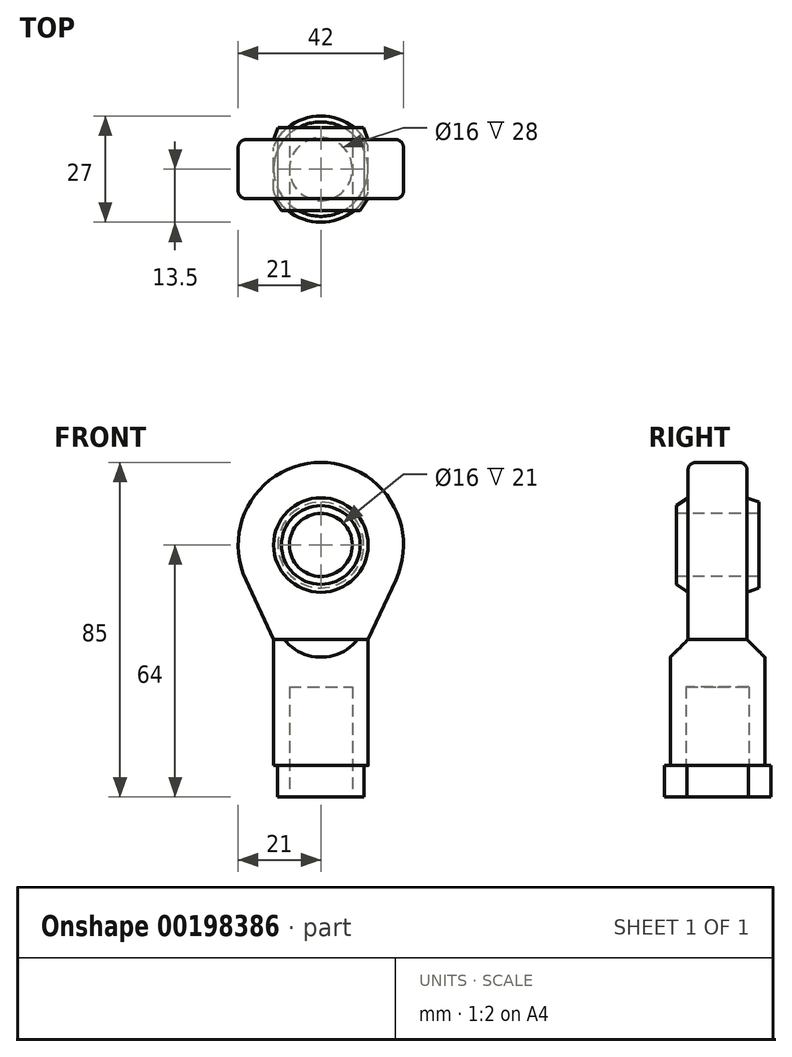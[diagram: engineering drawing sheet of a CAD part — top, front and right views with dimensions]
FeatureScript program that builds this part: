
annotation { "Feature Type Name" : "Feature", "Feature Type Description" : "" }
export const myFeature = defineFeature(function(context is Context, id is Id, definition is map)
    precondition{}
    {
        {
            var Q0;
            Q0=qCreatedBy(makeId("Top.planeOp"),FACE);
            var sketch = newSketch(context, id + "F0", { "sketchPlane" : qUnion([Q0])});
            skCircle(sketch, "E0", {"center": v(0, 0) * mm, "radius": 12 * mm});
            skSolve(sketch);
        }
        {
            var Q0;
            Q0 = qSketchRegion(id + "F0", true);
            extrude(context, id + "F1", {"entities" : qUnion([Q0]), "depth" : 64 * mm});
        }
        {
            var Q0;
            Q0=qCreatedBy(makeId("Top.planeOp"),FACE);
            var sketch = newSketch(context, id + "F2", { "sketchPlane" : qUnion([Q0])});
            skCircle(sketch, "E1", {"center": v(0, 0) * mm, "radius": 13.5 * mm});
            skSolve(sketch);
        }
        {
            var Q0;
            Q0 = qSketchRegion(id + "F2", true);
            extrude(context, id + "F3", {"entities" : qUnion([Q0]), "operationType" : NewBodyOperationType.ADD, "depth" : 8 * mm});
        }
        {
            var Q0;
            Q0=qCreatedBy(makeId("Front.planeOp"),FACE);
            var sketch = newSketch(context, id + "F4", { "sketchPlane" : qUnion([Q0])});
            skArc(sketch, "E2", {"start": v(19.04, 55.15) * mm, "mid": v(0, 85) * mm, "end": v(-19.04, 55.15) * mm});
            skLineSegment(sketch, "E3", {"start": v(12, 40) * mm, "end": v(12, 8) * mm});
            skLineSegment(sketch, "E4", {"start": v(-12, 8) * mm, "end": v(-12, 40) * mm});
            skLineSegment(sketch, "E5", {"start": v(-12, 40) * mm, "end": v(-19.04, 55.15) * mm});
            skLineSegment(sketch, "E6", {"start": v(12, 40) * mm, "end": v(19.04, 55.15) * mm});
            skLineSegment(sketch, "E7", {"start": v(-12, 40) * mm, "end": v(12, 40) * mm});
            skPoint(sketch, "E8.orphan", {"position": v(12, 64) * mm});
            skPoint(sketch, "E9.orphan", {"position": v(-12, 64) * mm});
            skSolve(sketch);
        }
        {
            var Q0;
            Q0 = qSketchRegion(id + "F4", true);
            extrude(context, id + "F5", {"entities" : qUnion([Q0]), "operationType" : NewBodyOperationType.ADD, "endBound" : BoundingType.SYMMETRIC, "depth" : 15 * mm});
        }
        {
            var Q0;
            Q0=qCreatedBy(makeId("Right.planeOp"),FACE);
            var sketch = newSketch(context, id + "F6", { "sketchPlane" : qUnion([Q0])});
            skLineSegment(sketch, "E10", {"start": v(-7.5, 64) * mm, "end": v(-7.5, 40) * mm});
            skLineSegment(sketch, "E11", {"start": v(-7.5, 40) * mm, "end": v(-12, 35.5) * mm});
            skLineSegment(sketch, "E12", {"start": v(-12, 35.5) * mm, "end": v(-12, 64) * mm});
            skLineSegment(sketch, "E13", {"start": v(-12, 64) * mm, "end": v(-7.5, 64) * mm});
            skLineSegment(sketch, "E14", {"start": v(7.5, 64) * mm, "end": v(7.5, 40) * mm});
            skLineSegment(sketch, "E15", {"start": v(7.5, 40) * mm, "end": v(12, 35.5) * mm});
            skLineSegment(sketch, "E16", {"start": v(12, 35.5) * mm, "end": v(12, 64) * mm});
            skLineSegment(sketch, "E17", {"start": v(12, 64) * mm, "end": v(7.5, 64) * mm});
            skSolve(sketch);
        }
        {
            var Q0;
            Q0 = qSketchRegion(id + "F6", true);
            extrude(context, id + "F7", {"entities" : qUnion([Q0]), "operationType" : NewBodyOperationType.REMOVE, "endBound" : BoundingType.SYMMETRIC, "depth" : 25 * mm});
        }
        {
            var Q0;
            Q0=qCreatedBy(makeId("Right.planeOp"),FACE);
            var sketch = newSketch(context, id + "F8", { "sketchPlane" : qUnion([Q0])});
            skLineSegment(sketch, "E18", {"start": v(-19.2, 64) * mm, "end": v(21.82, 64) * mm, "construction": true});
            skLineSegment(sketch, "E19", {"start": v(-10.5, 64) * mm, "end": v(-10.5, 74) * mm});
            skLineSegment(sketch, "E20", {"start": v(-10.5, 74) * mm, "end": v(-7.5, 76) * mm});
            skLineSegment(sketch, "E21", {"start": v(-7.5, 76) * mm, "end": v(7.5, 76) * mm});
            skLineSegment(sketch, "E22", {"start": v(7.5, 76) * mm, "end": v(10.5, 74.9) * mm});
            skLineSegment(sketch, "E23", {"start": v(10.5, 74.9) * mm, "end": v(10.5, 64) * mm});
            skLineSegment(sketch, "E24", {"start": v(10.5, 64) * mm, "end": v(-10.5, 64) * mm});
            skSolve(sketch);
        }
        {
            var Q0;
            Q0 = qSketchRegion(id + "F8", true);
            var Q1;
            Q1=sQuery(id+"F8.wireOp",EDGE,"E18");
            revolve(context, id + "F9", {"operationType" : NewBodyOperationType.ADD, "entities" : qUnion([Q0]), "axis" : qUnion([Q1]), "revolveType" : RevolveType.FULL});
        }
        {
            var Q0;
            Q0=makeQuery(id+"F9.opRevolve","SWEPT_FACE",FACE,{"disambiguationData":[OSD([sQuery(id+"F8.wireOp",EDGE,"E19")])]});
            var sketch = newSketch(context, id + "F10", { "sketchPlane" : qUnion([Q0])});
            skCircle(sketch, "E25", {"center": v(0, 64) * mm, "radius": 8 * mm});
            skSolve(sketch);
        }
        {
            var Q0;
            Q0 = qSketchRegion(id + "F10", true);
            extrude(context, id + "F11", {"entities" : qUnion([Q0]), "operationType" : NewBodyOperationType.REMOVE, "endBound" : BoundingType.THROUGH_ALL, "oppositeDirection" : true, "depth" : 25 * mm});
        }
        {
            var Q0;
            Q0=makeQuery(id+"F5.opExtrude","CAP_EDGE",EDGE,{"disambiguationData":[OSD([sQuery(id+"F4.wireOp",EDGE,"E6")])],"isStart":false});
            var Q1;
            Q1=makeQuery(id+"F5.opExtrude","CAP_EDGE",EDGE,{"disambiguationData":[OSD([sQuery(id+"F4.wireOp",EDGE,"E6")])],"isStart":true});
            fillet(context, id + "F12", {"entities" : qUnion([Q0, Q1]), "radius" : 2 * mm, "tangentPropagation" : true, "allowEdgeOverflow" : false});
        }
        {
            var Q0;
            Q0=makeQuery(id+"F3.boolean.opBoolean","MERGE",FACE,{"derivedFrom":[makeQuery(id+"F1.opExtrude","CAP_FACE",FACE,{"disambiguationData":[OSD([sQuery(id+"F0.wireOp",EDGE,"E0")])],"isStart":true}),makeQuery(id+"F3.opExtrude","CAP_FACE",FACE,{"disambiguationData":[OSD([sQuery(id+"F2.wireOp",EDGE,"E1")])],"isStart":true})]});
            var sketch = newSketch(context, id + "F13", { "sketchPlane" : qUnion([Q0])});
            skCircle(sketch, "E26", {"center": v(0, 0) * mm, "radius": 8 * mm});
            skSolve(sketch);
        }
        {
            var Q0;
            Q0 = qSketchRegion(id + "F13", true);
            extrude(context, id + "F14", {"entities" : qUnion([Q0]), "operationType" : NewBodyOperationType.REMOVE, "oppositeDirection" : true, "depth" : 28 * mm});
        }
        {
            var Q0;
            Q0=makeQuery(id+"F3.boolean.opBoolean","MERGE",FACE,{"derivedFrom":[makeQuery(id+"F1.opExtrude","CAP_FACE",FACE,{"disambiguationData":[OSD([sQuery(id+"F0.wireOp",EDGE,"E0")])],"isStart":true}),makeQuery(id+"F3.opExtrude","CAP_FACE",FACE,{"disambiguationData":[OSD([sQuery(id+"F2.wireOp",EDGE,"E1")])],"isStart":true})]});
            var sketch = newSketch(context, id + "F15", { "sketchPlane" : qUnion([Q0])});
            skArc(sketch, "E27.0", {"start": v(-11, 7.83) * mm, "mid": v(-13.5, 0) * mm, "end": v(-11, -7.83) * mm});
            skLineSegment(sketch, "E28", {"start": v(-11, -7.83) * mm, "end": v(-11, 7.83) * mm});
            skLineSegment(sketch, "E29", {"start": v(11, -7.83) * mm, "end": v(11, 7.83) * mm});
            skArc(sketch, "E30.trimOffspring", {"start": v(11, -7.83) * mm, "mid": v(13.5, 0) * mm, "end": v(11, 7.83) * mm});
            skSolve(sketch);
        }
        {
            var Q0;
            Q0 = qSketchRegion(id + "F15", true);
            var Q1;
            Q1=makeQuery(id+"F3.opExtrude","CAP_FACE",FACE,{"disambiguationData":[OSD([sQuery(id+"F2.wireOp",EDGE,"E1")])],"isStart":false});
            extrude(context, id + "F16", {"entities" : qUnion([Q0]), "operationType" : NewBodyOperationType.REMOVE, "endBound" : BoundingType.UP_TO_SURFACE, "oppositeDirection" : true, "endBoundEntityFace" : qUnion([Q1]), "depth" : 25 * mm});
        }
    });
